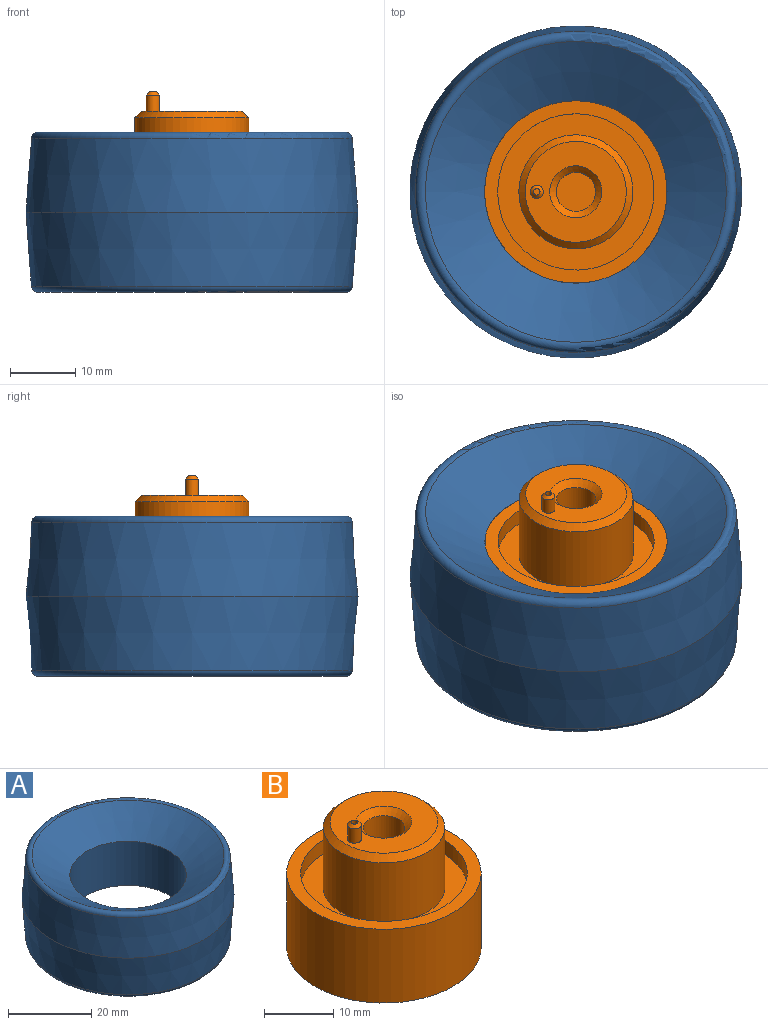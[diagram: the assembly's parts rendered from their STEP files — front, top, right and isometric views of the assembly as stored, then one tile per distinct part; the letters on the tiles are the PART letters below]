
ASSEMBLY  parts=2 mates=1
PART A: 7 faces, bbox 53.3x53.3x24.6 mm
  f0: cone r=25.5mm half-angle=4.4deg, axis (0,0,-1), area 1794.4mm2, adj f1,f6
  f1: cone r=25.5mm half-angle=4.4deg, axis (0,0,1), area 1794.4mm2, adj f0,f5
  f2: cone r=24.5mm half-angle=58.2deg, axis (0,0,-1), area 1247.9mm2, adj f3,f5
  f3: cylinder r=14mm len=28mm, axis (0,0,1), area 1143.5mm2, adj f2,f4
  f4: cone r=24.5mm half-angle=58.2deg, axis (0,0,1), area 1247.9mm2, adj f3,f6
  f5: torus R=23.63mm, axis (0,0,-1), area 309mm2, adj f1,f2
  f6: torus R=23.63mm, axis (0,0,-1), area 309mm2, adj f0,f4
PART B: 17 faces, bbox 28x28x25 mm
  f0: plane 28x28mm, normal (0,0,1), area 163.4mm2, adj f1,f10
  f1: cylinder r=12mm len=24mm, axis (0,0,-1), area 188.5mm2, adj f0,f2
  f2: plane 24x24mm, normal (0,0,1), area 211.9mm2, adj f1,f3
  f3: cylinder r=8.75mm len=17.5mm, axis (0,0,-1), area 577.3mm2, adj f2,f12
  f4: plane 15.5x15.5mm, normal (0,0,1), area 135.3mm2, adj f11,f12,f14
  f5: cylinder r=3mm len=18mm, axis (0,0,-1), area 339.3mm2, adj f6,f11
  f6: plane 6x6mm, normal (0,0,1), area 28.3mm2, adj f5
  f7: plane 24x24mm, normal (0,0,-1), area 452.4mm2, adj f8
  f8: cylinder r=12mm len=24mm, axis (0,0,-1), area 150.8mm2, adj f7,f9
  f9: plane 28x28mm, normal (0,0,-1), area 163.4mm2, adj f8,f10
  f10: cylinder r=14mm len=28mm, axis (0,0,-1), area 1143.5mm2, adj f0,f9
  f11: cone r=4mm half-angle=45deg, axis (0,0,1), area 31.1mm2, adj f4,f5
  f12: cone r=8.75mm half-angle=45deg, axis (0,0,-1), area 73.3mm2, adj f3,f4
  f13: cylinder r=0.5mm len=3mm, axis (0,0,-1), area 9.4mm2, adj f15,f16
  f14: cylinder r=1mm len=2.5mm, axis (0,0,-1), area 15.7mm2, adj f4,f16
  f15: plane 1x1mm, normal (0,0,1), area 0.8mm2, adj f13
  f16: cone r=0.5mm half-angle=45deg, axis (0,0,-1), area 3.3mm2, adj f13,f14
PLACE A t=(2.18,2.18,7.95)mm
PLACE B t=(2.18,2.18,3.45)mm
MATE fastened A.f0 <-> B.f1  axis (0,0,1) through (2.18,2.18,7.95)mm
